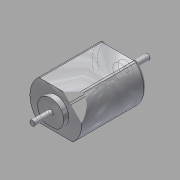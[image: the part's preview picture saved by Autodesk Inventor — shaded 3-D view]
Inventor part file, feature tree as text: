
AUTODESK INVENTOR PART (.ipt)
format: ipt  version: 2015 (Build 190159000, 159)  size: 141,824 bytes
history: native  units: in
note: dims shown in document units (in); Inventor stores cm internally (conversion verified against a paired STEP export)
features: sketch x5, other x3
ambient origin geometry x8: Origin, YZ Plane, XZ Plane, XY Plane, X Axis, Y Axis, Z Axis, Center Point
bodies: Solid1 (feature_tree)
feature tree (8):
  other  "motor_MIR3.ipt"
  other  "Solid1::motor_MIR3.ipt"
  other  "TaggingFeature1"
  sketch  "Sketch1"  dims[d0=0.3937in]
  sketch  "Sketch2"
  sketch  "Sketch3"
  sketch  "Sketch4"
  sketch  "Sketch5"
